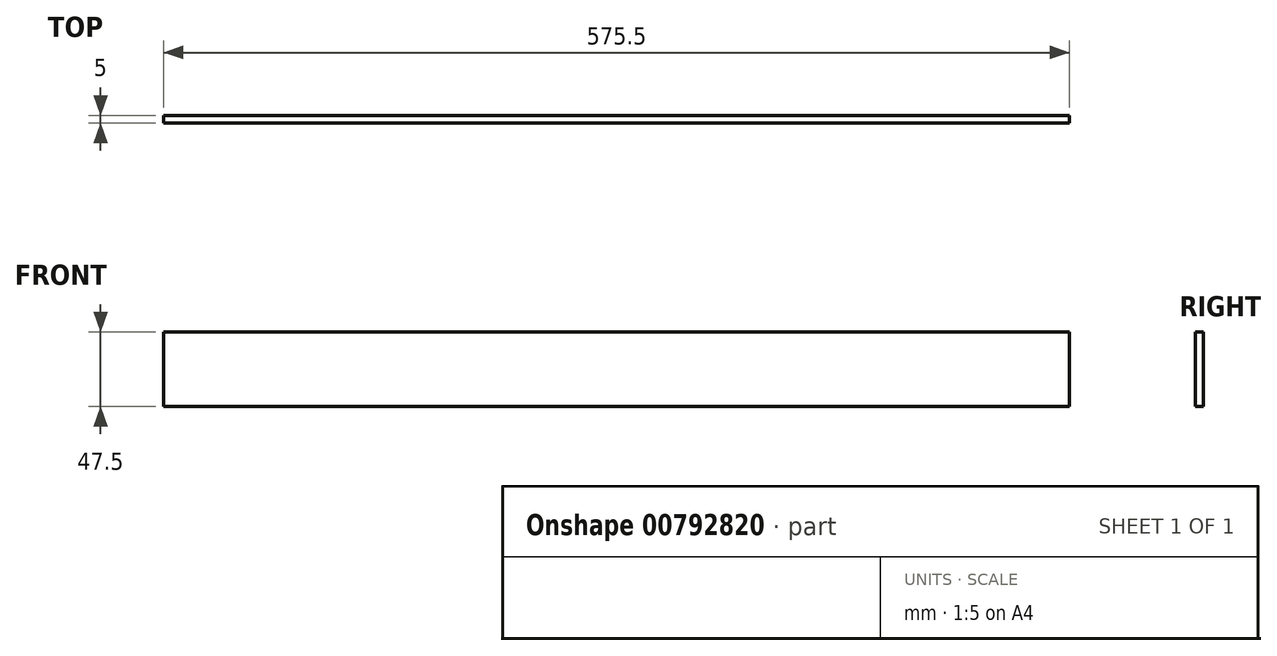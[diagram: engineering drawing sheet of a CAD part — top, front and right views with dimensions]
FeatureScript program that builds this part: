
annotation { "Feature Type Name" : "Feature", "Feature Type Description" : "" }
export const myFeature = defineFeature(function(context is Context, id is Id, definition is map)
    precondition{}
    {
        {
            var Q0;
            Q0=qCreatedBy(makeId("Front.planeOp"),FACE);
            var sketch = newSketch(context, id + "F0", { "sketchPlane" : qUnion([Q0])});
            skLineSegment(sketch, "E0.bottom", {"start": v(287.75, -23.75) * mm, "end": v(-287.75, -23.75) * mm});
            skLineSegment(sketch, "E0.top", {"start": v(287.75, 23.75) * mm, "end": v(-287.75, 23.75) * mm});
            skLineSegment(sketch, "E0.left", {"start": v(287.75, -23.75) * mm, "end": v(287.75, 23.75) * mm});
            skLineSegment(sketch, "E0.right", {"start": v(-287.75, -23.75) * mm, "end": v(-287.75, 23.75) * mm});
            skPoint(sketch, "E0.middle", {"position": v(0, 0) * mm});
            skSolve(sketch);
        }
        {
            var Q0;
            Q0=makeQuery(id+"F0.imprint","IMPRINT",FACE,{"disambiguationData":[TD([[makeQuery(id+"F0.imprint","IMPRINT",EDGE,{"derivedFrom":sQuery(id+"F0.wireOp",EDGE,"E0.bottom")}),-1.0]])]});
            extrude(context, id + "F1", {"entities" : qUnion([Q0]), "depth" : 5 * mm, "offsetDistance" : 25 * mm});
        }
    });
